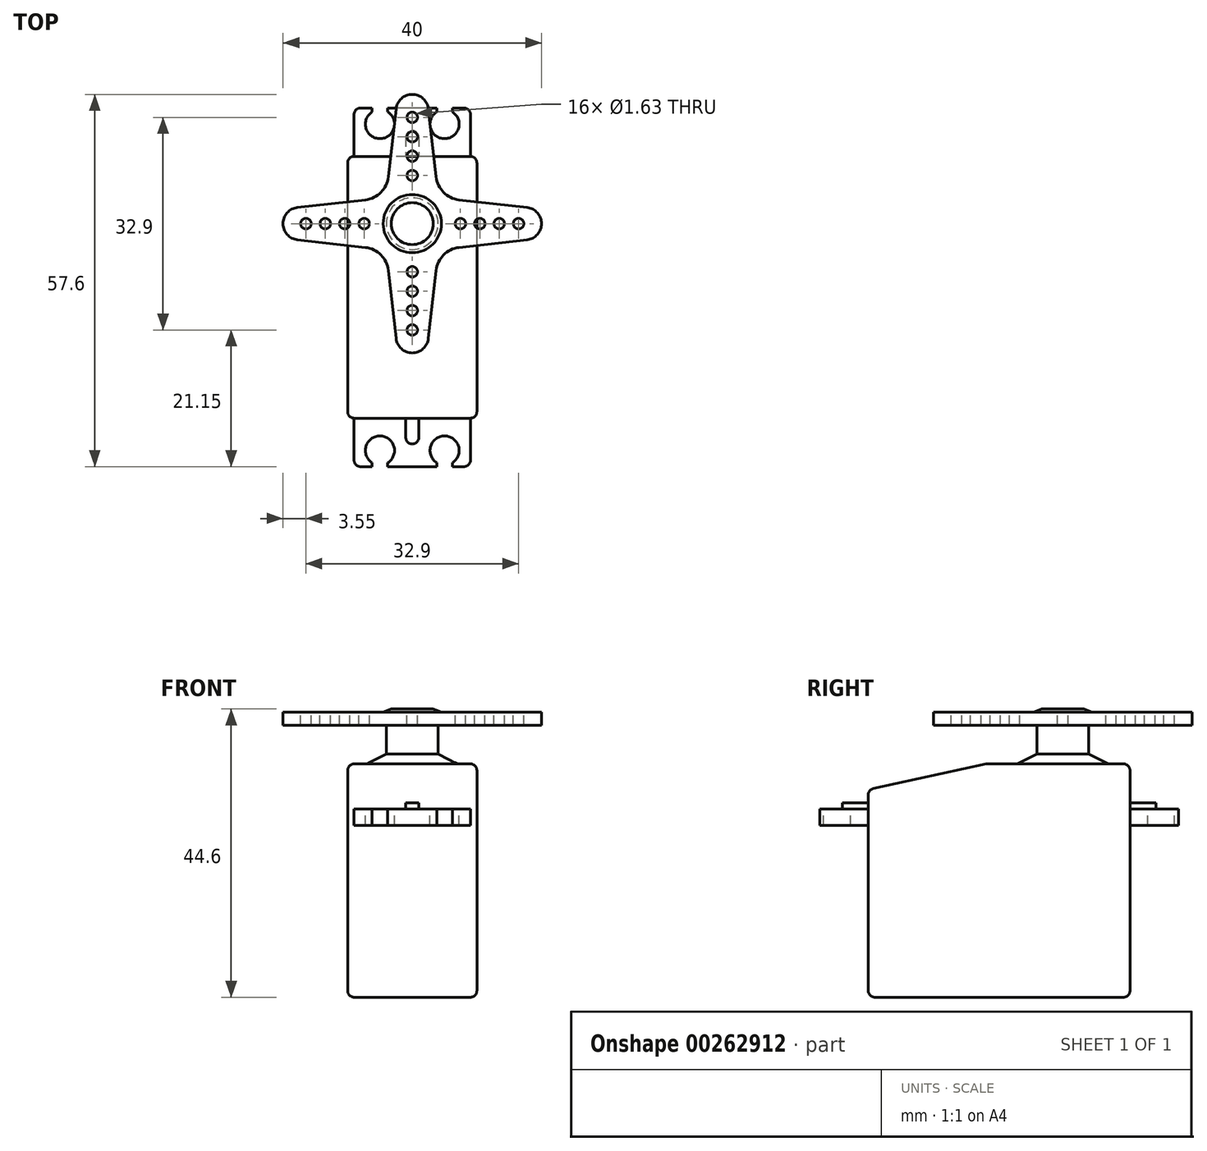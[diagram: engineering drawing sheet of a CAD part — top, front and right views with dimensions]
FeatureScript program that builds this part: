
annotation { "Feature Type Name" : "Feature", "Feature Type Description" : "" }
export const myFeature = defineFeature(function(context is Context, id is Id, definition is map)
    precondition{}
    {
        {
            var Q0;
            Q0=qCreatedBy(makeId("Right.planeOp"),FACE);
            var sketch = newSketch(context, id + "F0", { "sketchPlane" : qUnion([Q0])});
            skLineSegment(sketch, "E0.bottom", {"start": v(-20.25, 0) * mm, "end": v(20.25, 0) * mm});
            skLineSegment(sketch, "E0.top", {"start": v(-20.25, 36.1) * mm, "end": v(20.25, 36.1) * mm});
            skLineSegment(sketch, "E0.left", {"start": v(-20.25, 0) * mm, "end": v(-20.25, 36.1) * mm});
            skLineSegment(sketch, "E0.right", {"start": v(20.25, 0) * mm, "end": v(20.25, 36.1) * mm});
            skLineSegment(sketch, "E1.bottom", {"start": v(20.25, 29.1) * mm, "end": v(27.75, 29.1) * mm});
            skLineSegment(sketch, "E1.top", {"start": v(20.25, 26.6) * mm, "end": v(27.75, 26.6) * mm});
            skLineSegment(sketch, "E1.left", {"start": v(20.25, 29.1) * mm, "end": v(20.25, 26.6) * mm});
            skLineSegment(sketch, "E1.right", {"start": v(27.75, 29.1) * mm, "end": v(27.75, 26.6) * mm});
            skLineSegment(sketch, "E2.bottom", {"start": v(0, 36.1) * mm, "end": v(0, 36.1) * mm});
            skLineSegment(sketch, "E2.top", {"start": v(0, 0) * mm, "end": v(0, 0) * mm});
            skLineSegment(sketch, "E2.left", {"start": v(0, 36.1) * mm, "end": v(0, 0) * mm, "construction": true});
            skLineSegment(sketch, "E2.right", {"start": v(0, 36.1) * mm, "end": v(0, 0) * mm, "construction": true});
            skLineSegment(sketch, "E3.MirrorCS", {"start": v(-20.25, 29.1) * mm, "end": v(-27.75, 29.1) * mm});
            skLineSegment(sketch, "E4.MirrorCS", {"start": v(-27.75, 29.1) * mm, "end": v(-27.75, 26.6) * mm});
            skLineSegment(sketch, "E5.MirrorCS", {"start": v(-20.25, 26.6) * mm, "end": v(-27.75, 26.6) * mm});
            skLineSegment(sketch, "E6.MirrorCS", {"start": v(-20.25, 29.1) * mm, "end": v(-20.25, 26.6) * mm});
            skLineSegment(sketch, "E7", {"start": v(-20.25, 32.1) * mm, "end": v(-1.95, 36.1) * mm});
            skSolve(sketch);
        }
        {
            var Q0;
            {var subQ3=sQuery(id+"F0.wireOp",EDGE,"E0.bottom");Q0=makeQuery(id+"F0.imprint","IMPRINT",FACE,{"disambiguationData":[TD([[makeQuery(id+"F0.imprint","IMPRINT",EDGE,{"derivedFrom":subQ3}),1.0]])]});}
            extrude(context, id + "F1", {"entities" : qUnion([Q0]), "endBound" : BoundingType.SYMMETRIC, "depth" : 20 * mm, "hasSecondDirection" : true, "secondDirectionOppositeDirection" : true, "secondDirectionDepth" : 25 * mm});
        }
        {
            var Q0;
            Q0=makeQuery(id+"F0.imprint","IMPRINT",FACE,{"disambiguationData":[TD([[makeQuery(id+"F0.imprint","IMPRINT",EDGE,{"derivedFrom":sQuery(id+"F0.wireOp",EDGE,"E3.MirrorCS")}),1.0]])]});
            var Q1;
            Q1=makeQuery(id+"F0.imprint","IMPRINT",FACE,{"disambiguationData":[TD([[makeQuery(id+"F0.imprint","IMPRINT",EDGE,{"derivedFrom":sQuery(id+"F0.wireOp",EDGE,"E1.bottom")}),-1.0]])]});
            extrude(context, id + "F2", {"entities" : qUnion([Q0, Q1]), "operationType" : NewBodyOperationType.ADD, "endBound" : BoundingType.SYMMETRIC, "depth" : 18 * mm});
        }
        {
            var Q0;
            Q0=makeQuery(id+"F2.opExtrude","SWEPT_FACE",FACE,{"disambiguationData":[OSD([sQuery(id+"F0.wireOp",EDGE,"E3.MirrorCS")])]});
            var sketch = newSketch(context, id + "F3", { "sketchPlane" : qUnion([Q0])});
            skLineSegment(sketch, "E8.0", {"start": v(-10, -20.25) * mm, "end": v(-10, -1.95) * mm, "construction": true});
            skLineSegment(sketch, "E9.0", {"start": v(-10, -1.95) * mm, "end": v(-10, 20.25) * mm, "construction": true});
            skLineSegment(sketch, "E10.0", {"start": v(10, 20.25) * mm, "end": v(-10, 20.25) * mm, "construction": true});
            skLineSegment(sketch, "E11.0", {"start": v(10, -1.95) * mm, "end": v(10, 20.25) * mm, "construction": true});
            skLineSegment(sketch, "E12.0", {"start": v(10, -20.25) * mm, "end": v(10, -1.95) * mm, "construction": true});
            skLineSegment(sketch, "E13.0", {"start": v(10, -20.25) * mm, "end": v(-10, -20.25) * mm, "construction": true});
            skLineSegment(sketch, "E14", {"start": v(-10, -20.25) * mm, "end": v(10, 20.25) * mm, "construction": true});
            skLineSegment(sketch, "E15", {"start": v(-10, 20.25) * mm, "end": v(10, -20.25) * mm, "construction": true});
            skLineSegment(sketch, "E16", {"start": v(-10, 0) * mm, "end": v(10, 0) * mm, "construction": true});
            skPoint(sketch, "E16.endSnap0", {"position": v(0, 0) * mm});
            skLineSegment(sketch, "E17", {"start": v(0, -20.25) * mm, "end": v(0, 20.25) * mm, "construction": true});
            skCircle(sketch, "E18", {"center": v(-5, -25.25) * mm, "radius": 2.25 * mm});
            skLineSegment(sketch, "E19", {"start": v(-6.2, -27.75) * mm, "end": v(-3.8, -27.75) * mm});
            skLineSegment(sketch, "E20", {"start": v(-3.8, -27.75) * mm, "end": v(-3.8, -27.15) * mm});
            skLineSegment(sketch, "E21", {"start": v(-6.2, -27.75) * mm, "end": v(-6.2, -27.15) * mm});
            skLineSegment(sketch, "E22.MirrorCS", {"start": v(-6.2, 27.75) * mm, "end": v(-6.2, 27.15) * mm});
            skLineSegment(sketch, "E23.MirrorCS", {"start": v(-6.2, 27.75) * mm, "end": v(-3.8, 27.75) * mm});
            skLineSegment(sketch, "E24.MirrorCS", {"start": v(-3.8, 27.75) * mm, "end": v(-3.8, 27.15) * mm});
            skCircle(sketch, "E25.MirrorC", {"center": v(-5, 25.25) * mm, "radius": 2.25 * mm});
            skLineSegment(sketch, "E26.MirrorCS", {"start": v(3.8, -27.75) * mm, "end": v(3.8, -27.15) * mm});
            skLineSegment(sketch, "E27.MirrorCS", {"start": v(3.8, 27.75) * mm, "end": v(3.8, 27.15) * mm});
            skLineSegment(sketch, "E28.MirrorCS", {"start": v(6.2, 27.75) * mm, "end": v(6.2, 27.15) * mm});
            skLineSegment(sketch, "E29.MirrorCS", {"start": v(6.2, -27.75) * mm, "end": v(6.2, -27.15) * mm});
            skLineSegment(sketch, "E30.MirrorCS", {"start": v(6.2, 27.75) * mm, "end": v(3.8, 27.75) * mm});
            skLineSegment(sketch, "E31.MirrorCS", {"start": v(6.2, -27.75) * mm, "end": v(3.8, -27.75) * mm});
            skCircle(sketch, "E32.MirrorC", {"center": v(5, 25.25) * mm, "radius": 2.25 * mm});
            skCircle(sketch, "E33.MirrorC", {"center": v(5, -25.25) * mm, "radius": 2.25 * mm});
            skSolve(sketch);
        }
        {
            var Q0;
            Q0=qSketchRegion(id+"F3",true);
            extrude(context, id + "F4", {"entities" : qUnion([Q0]), "operationType" : NewBodyOperationType.REMOVE, "oppositeDirection" : true, "depth" : 25 * mm});
        }
        {
            var Q0;
            Q0=makeQuery(id+"F2.opExtrude","SWEPT_FACE",FACE,{"disambiguationData":[OSD([sQuery(id+"F0.wireOp",EDGE,"E3.MirrorCS")])]});
            var sketch = newSketch(context, id + "F5", { "sketchPlane" : qUnion([Q0])});
            skLineSegment(sketch, "E34.0", {"start": v(10, -20.25) * mm, "end": v(-10, -20.25) * mm, "construction": true});
            skLineSegment(sketch, "E35.0", {"start": v(10, 20.25) * mm, "end": v(-10, 20.25) * mm, "construction": true});
            skLineSegment(sketch, "E36", {"start": v(0, -20.25) * mm, "end": v(0, 20.25) * mm, "construction": true});
            skLineSegment(sketch, "E37.rect.bottom", {"start": v(1, 23.25) * mm, "end": v(-1, 23.25) * mm});
            skLineSegment(sketch, "E37.rect.top", {"start": v(1, -23.25) * mm, "end": v(-1, -23.25) * mm});
            skLineSegment(sketch, "E37.rect.left", {"start": v(1, 23.25) * mm, "end": v(1, -23.25) * mm});
            skLineSegment(sketch, "E37.rect.right", {"start": v(-1, 23.25) * mm, "end": v(-1, -23.25) * mm});
            skPoint(sketch, "E37.rect.middle", {"position": v(0, 0) * mm});
            skArc(sketch, "E38", {"start": v(1, 23.25) * mm, "mid": v(0, 24.25) * mm, "end": v(-1, 23.25) * mm});
            skArc(sketch, "E39", {"start": v(-1, -23.25) * mm, "mid": v(0, -24.25) * mm, "end": v(1, -23.25) * mm});
            skPoint(sketch, "E40", {"position": v(0, 24.25) * mm});
            skSolve(sketch);
        }
        {
            var Q0;
            Q0=qSketchRegion(id+"F5",true);
            extrude(context, id + "F6", {"entities" : qUnion([Q0]), "operationType" : NewBodyOperationType.ADD, "depth" : 1 * mm});
        }
        {
            var Q0;
            Q0=qCreatedBy(makeId("Right.planeOp"),FACE);
            var sketch = newSketch(context, id + "F7", { "sketchPlane" : qUnion([Q0])});
            skLineSegment(sketch, "E41.0", {"start": v(-1.95, 36.1) * mm, "end": v(20.25, 36.1) * mm, "construction": true});
            skLineSegment(sketch, "E42.0", {"start": v(-20.25, 0) * mm, "end": v(-20.25, 32.1) * mm, "construction": true});
            skLineSegment(sketch, "E43.0", {"start": v(20.25, 0) * mm, "end": v(20.25, 36.1) * mm, "construction": true});
            skLineSegment(sketch, "E44", {"start": v(9.85, 53.58) * mm, "end": v(9.85, 24.34) * mm, "construction": true});
            skLineSegment(sketch, "E45", {"start": v(16.85, 36.1) * mm, "end": v(13.85, 37.6) * mm});
            skLineSegment(sketch, "E46", {"start": v(13.85, 37.6) * mm, "end": v(13.85, 42.1) * mm});
            skLineSegment(sketch, "E47", {"start": v(13.85, 42.1) * mm, "end": v(29.85, 42.1) * mm});
            skLineSegment(sketch, "E48", {"start": v(29.85, 42.1) * mm, "end": v(29.85, 44.1) * mm});
            skLineSegment(sketch, "E49", {"start": v(29.85, 44.1) * mm, "end": v(14.35, 44.1) * mm});
            skLineSegment(sketch, "E50", {"start": v(14.35, 44.1) * mm, "end": v(13.1, 44.6) * mm});
            skLineSegment(sketch, "E51", {"start": v(13.1, 44.6) * mm, "end": v(9.85, 44.6) * mm});
            skLineSegment(sketch, "E52", {"start": v(9.85, 44.6) * mm, "end": v(9.85, 36.1) * mm});
            skLineSegment(sketch, "E53", {"start": v(9.85, 36.1) * mm, "end": v(16.85, 36.1) * mm});
            skSolve(sketch);
        }
        {
            var Q0;
            Q0=qSketchRegion(id+"F7",true);
            var Q1;
            Q1=sQuery(id+"F7.wireOp",EDGE,"E44");
            revolve(context, id + "F8", {"operationType" : NewBodyOperationType.ADD, "entities" : qUnion([Q0]), "axis" : qUnion([Q1]), "revolveType" : RevolveType.FULL});
        }
        {
            var Q0;
            Q0=makeQuery(id+"F8.opRevolve","SWEPT_FACE",FACE,{"disambiguationData":[OSD([sQuery(id+"F7.wireOp",EDGE,"E49")])]});
            var sketch = newSketch(context, id + "F9", { "sketchPlane" : qUnion([Q0])});
            skPoint(sketch, "E54", {"position": v(0, 9.85) * mm});
            skCircle(sketch, "E55", {"center": v(0, 17.3) * mm, "radius": 0.81 * mm});
            skCircle(sketch, "E56", {"center": v(0, 20.3) * mm, "radius": 0.81 * mm});
            skCircle(sketch, "E57", {"center": v(0, 23.3) * mm, "radius": 0.81 * mm});
            skCircle(sketch, "E58", {"center": v(0, 26.3) * mm, "radius": 0.81 * mm});
            skCircle(sketch, "E59.1.0", {"center": v(-16.45, 9.85) * mm, "radius": 0.81 * mm});
            skCircle(sketch, "E59.1.1", {"center": v(-13.45, 9.85) * mm, "radius": 0.81 * mm});
            skCircle(sketch, "E59.1.2", {"center": v(-10.45, 9.85) * mm, "radius": 0.81 * mm});
            skCircle(sketch, "E59.1.3", {"center": v(-7.45, 9.85) * mm, "radius": 0.81 * mm});
            skCircle(sketch, "E59.2.0", {"center": v(0, -6.6) * mm, "radius": 0.81 * mm});
            skCircle(sketch, "E59.2.1", {"center": v(0, -3.6) * mm, "radius": 0.81 * mm});
            skCircle(sketch, "E59.2.2", {"center": v(0, -0.6) * mm, "radius": 0.81 * mm});
            skCircle(sketch, "E59.2.3", {"center": v(0, 2.4) * mm, "radius": 0.81 * mm});
            skCircle(sketch, "E59.3.0", {"center": v(16.45, 9.85) * mm, "radius": 0.81 * mm});
            skCircle(sketch, "E59.3.1", {"center": v(13.45, 9.85) * mm, "radius": 0.81 * mm});
            skCircle(sketch, "E59.3.2", {"center": v(10.45, 9.85) * mm, "radius": 0.81 * mm});
            skCircle(sketch, "E59.3.3", {"center": v(7.45, 9.85) * mm, "radius": 0.81 * mm});
            skSolve(sketch);
        }
        {
            var Q0;
            Q0=qSketchRegion(id+"F9",true);
            extrude(context, id + "F10", {"entities" : qUnion([Q0]), "operationType" : NewBodyOperationType.REMOVE, "endBound" : BoundingType.UP_TO_NEXT, "oppositeDirection" : true, "depth" : 25 * mm});
        }
        {
            var Q0;
            Q0=makeQuery(id+"F8.opRevolve","SWEPT_FACE",FACE,{"disambiguationData":[OSD([sQuery(id+"F7.wireOp",EDGE,"E49")])]});
            var sketch = newSketch(context, id + "F11", { "sketchPlane" : qUnion([Q0])});
            skPoint(sketch, "E60", {"position": v(0, 9.85) * mm});
            skLineSegment(sketch, "E61", {"start": v(0, 9.85) * mm, "end": v(0, 29.85) * mm, "construction": true});
            skLineSegment(sketch, "E62", {"start": v(0, 9.85) * mm, "end": v(-14.14, 24) * mm, "construction": true});
            skLineSegment(sketch, "E63", {"start": v(0, 9.85) * mm, "end": v(14.14, 24) * mm, "construction": true});
            skLineSegment(sketch, "E64", {"start": v(-3.69, 17.1) * mm, "end": v(-2.5, 27.62) * mm});
            skArc(sketch, "E65", {"start": v(0, 29.85) * mm, "mid": v(-1.68, 29.21) * mm, "end": v(-2.5, 27.62) * mm});
            skArc(sketch, "E66", {"start": v(-4.84, 14.7) * mm, "mid": v(-4.06, 15.8) * mm, "end": v(-3.69, 17.1) * mm});
            skArc(sketch, "E67.MirrorCS", {"start": v(4.84, 14.7) * mm, "mid": v(4.06, 15.8) * mm, "end": v(3.69, 17.1) * mm});
            skLineSegment(sketch, "E68.MirrorCS", {"start": v(3.69, 17.1) * mm, "end": v(2.5, 27.62) * mm});
            skArc(sketch, "E69.MirrorCS", {"start": v(0, 29.85) * mm, "mid": v(1.68, 29.21) * mm, "end": v(2.5, 27.62) * mm});
            skArc(sketch, "E70.1.0", {"start": v(-4.84, 5) * mm, "mid": v(-5.95, 5.79) * mm, "end": v(-7.24, 6.16) * mm});
            skLineSegment(sketch, "E70.1.1", {"start": v(-7.24, 6.16) * mm, "end": v(-17.77, 7.35) * mm});
            skArc(sketch, "E70.1.2", {"start": v(-20, 9.85) * mm, "mid": v(-19.36, 8.17) * mm, "end": v(-17.77, 7.35) * mm});
            skArc(sketch, "E70.1.3", {"start": v(-20, 9.85) * mm, "mid": v(-19.36, 11.53) * mm, "end": v(-17.77, 12.35) * mm});
            skLineSegment(sketch, "E70.1.4", {"start": v(-7.24, 13.54) * mm, "end": v(-17.77, 12.35) * mm});
            skArc(sketch, "E70.1.5", {"start": v(-4.84, 14.7) * mm, "mid": v(-5.95, 13.91) * mm, "end": v(-7.24, 13.54) * mm});
            skArc(sketch, "E70.2.0", {"start": v(4.84, 5) * mm, "mid": v(4.06, 3.9) * mm, "end": v(3.69, 2.6) * mm});
            skLineSegment(sketch, "E70.2.1", {"start": v(3.69, 2.6) * mm, "end": v(2.5, -7.92) * mm});
            skArc(sketch, "E70.2.2", {"start": v(0, -10.15) * mm, "mid": v(1.68, -9.51) * mm, "end": v(2.5, -7.92) * mm});
            skArc(sketch, "E70.2.3", {"start": v(0, -10.15) * mm, "mid": v(-1.68, -9.51) * mm, "end": v(-2.5, -7.92) * mm});
            skLineSegment(sketch, "E70.2.4", {"start": v(-3.69, 2.6) * mm, "end": v(-2.5, -7.92) * mm});
            skArc(sketch, "E70.2.5", {"start": v(-4.84, 5) * mm, "mid": v(-4.06, 3.9) * mm, "end": v(-3.69, 2.6) * mm});
            skArc(sketch, "E70.3.0", {"start": v(4.84, 14.7) * mm, "mid": v(5.95, 13.91) * mm, "end": v(7.24, 13.54) * mm});
            skLineSegment(sketch, "E70.3.1", {"start": v(7.24, 13.54) * mm, "end": v(17.77, 12.35) * mm});
            skArc(sketch, "E70.3.2", {"start": v(20, 9.85) * mm, "mid": v(19.36, 11.53) * mm, "end": v(17.77, 12.35) * mm});
            skArc(sketch, "E70.3.3", {"start": v(20, 9.85) * mm, "mid": v(19.36, 8.17) * mm, "end": v(17.77, 7.35) * mm});
            skLineSegment(sketch, "E70.3.4", {"start": v(7.24, 6.16) * mm, "end": v(17.77, 7.35) * mm});
            skArc(sketch, "E70.3.5", {"start": v(4.84, 5) * mm, "mid": v(5.95, 5.79) * mm, "end": v(7.24, 6.16) * mm});
            skCircle(sketch, "E71", {"center": v(0, 9.85) * mm, "radius": 26.3 * mm});
            skSolve(sketch);
        }
        {
            var Q0;
            Q0=qSketchRegion(id+"F11",true);
            var Q1;
            Q1=makeQuery(id+"F8.opRevolve","SWEPT_FACE",FACE,{"disambiguationData":[OSD([sQuery(id+"F7.wireOp",EDGE,"E47")])]});
            extrude(context, id + "F12", {"entities" : qUnion([Q0]), "operationType" : NewBodyOperationType.REMOVE, "endBound" : BoundingType.UP_TO_SURFACE, "oppositeDirection" : true, "endBoundEntityFace" : qUnion([Q1]), "depth" : 25 * mm});
        }
        {
            var Q0;
            Q0=makeQuery(id+"F1.opExtrude","CAP_FACE",FACE,{"disambiguationData":[OSD([sQuery(id+"F0.wireOp",EDGE,"E0.bottom"),sQuery(id+"F0.wireOp",EDGE,"E0.top"),sQuery(id+"F0.wireOp",EDGE,"E0.left"),sQuery(id+"F0.wireOp",EDGE,"E0.right"),sQuery(id+"F0.wireOp",EDGE,"E1.left"),sQuery(id+"F0.wireOp",EDGE,"E6.MirrorCS"),sQuery(id+"F0.wireOp",EDGE,"E7")])],"isStart":false});
            var Q1;
            Q1=makeQuery(id+"F1.opExtrude","CAP_FACE",FACE,{"disambiguationData":[OSD([sQuery(id+"F0.wireOp",EDGE,"E0.bottom"),sQuery(id+"F0.wireOp",EDGE,"E0.top"),sQuery(id+"F0.wireOp",EDGE,"E0.left"),sQuery(id+"F0.wireOp",EDGE,"E0.right"),sQuery(id+"F0.wireOp",EDGE,"E1.left"),sQuery(id+"F0.wireOp",EDGE,"E6.MirrorCS"),sQuery(id+"F0.wireOp",EDGE,"E7")])],"isStart":true});
            var Q2;
            Q2=makeQuery(id+"F1.opExtrude","SWEPT_FACE",FACE,{"disambiguationData":[OSD([sQuery(id+"F0.wireOp",EDGE,"E0.bottom")])]});
            var Q3;
            Q3=makeQuery(id+"F1.opExtrude","SWEPT_FACE",FACE,{"disambiguationData":[OSD([sQuery(id+"F0.wireOp",EDGE,"E7")])]});
            var Q4;
            Q4=makeQuery(id+"F1.opExtrude","SWEPT_FACE",FACE,{"disambiguationData":[OSD([sQuery(id+"F0.wireOp",EDGE,"E0.top")])]});
            var Q5;
            Q5=makeQuery(id+"F2.opExtrude","CAP_EDGE",EDGE,{"disambiguationData":[OSD([sQuery(id+"F0.wireOp",EDGE,"E4.MirrorCS")])],"isStart":false});
            var Q6;
            Q6=makeQuery(id+"F2.opExtrude","CAP_EDGE",EDGE,{"disambiguationData":[OSD([sQuery(id+"F0.wireOp",EDGE,"E4.MirrorCS")])],"isStart":true});
            var Q7;
            Q7=makeQuery(id+"F2.opExtrude","CAP_EDGE",EDGE,{"disambiguationData":[OSD([sQuery(id+"F0.wireOp",EDGE,"E1.right")])],"isStart":false});
            var Q8;
            Q8=makeQuery(id+"F2.opExtrude","CAP_EDGE",EDGE,{"disambiguationData":[OSD([sQuery(id+"F0.wireOp",EDGE,"E1.right")])],"isStart":true});
            fillet(context, id + "F13", {"entities" : qUnion([Q0, Q1, Q2, Q3, Q4, Q5, Q6, Q7, Q8]), "radius" : 1 * mm, "tangentPropagation" : true, "allowEdgeOverflow" : false});
        }
    });
